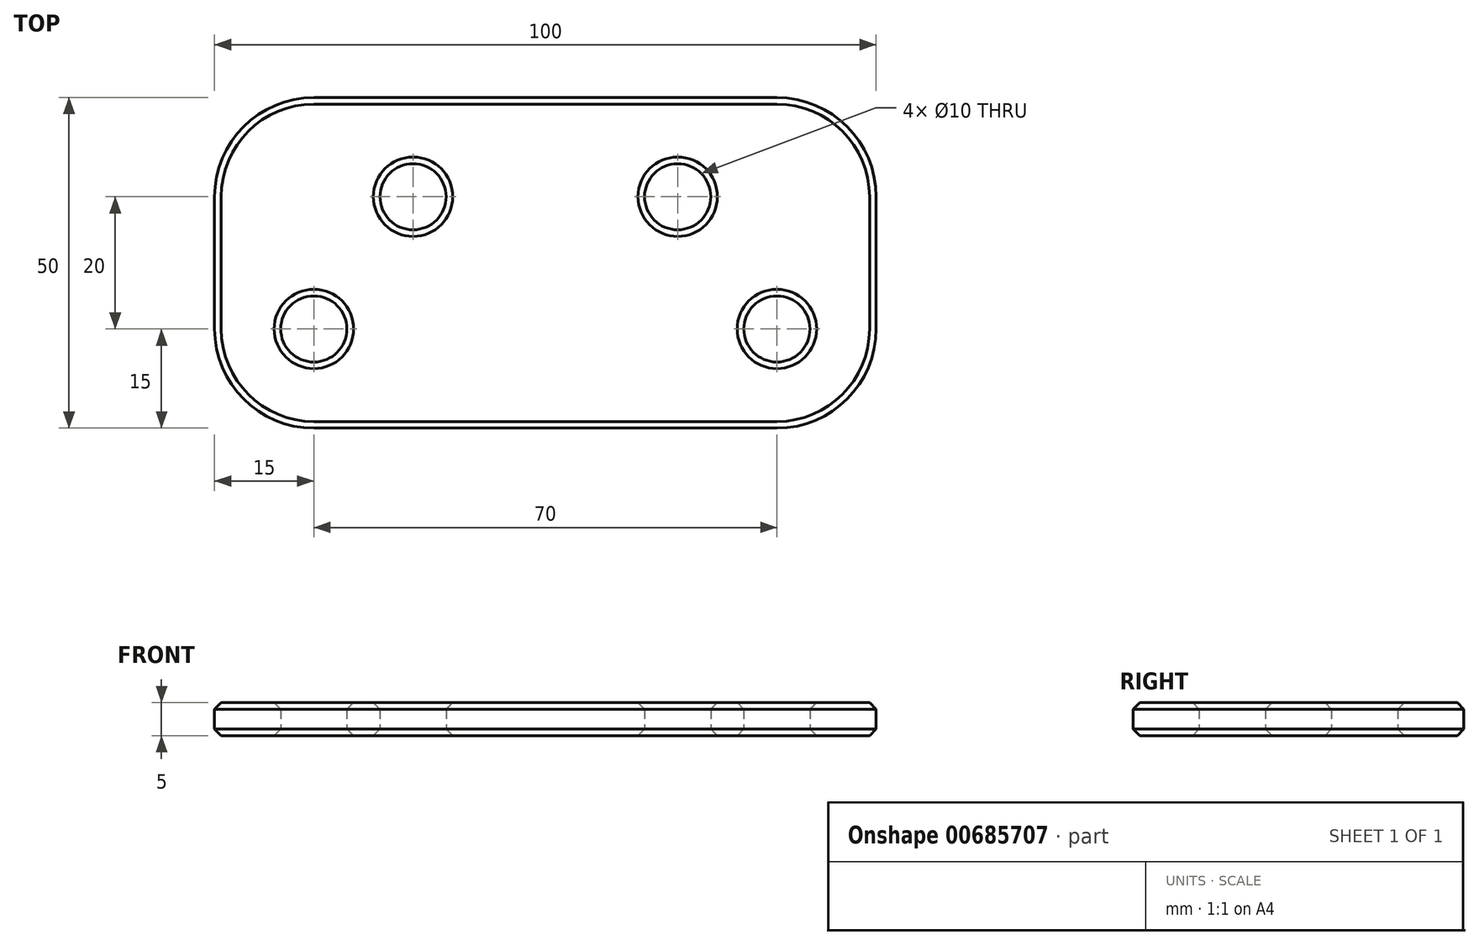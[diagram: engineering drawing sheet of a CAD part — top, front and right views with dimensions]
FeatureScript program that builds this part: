
annotation { "Feature Type Name" : "Feature", "Feature Type Description" : "" }
export const myFeature = defineFeature(function(context is Context, id is Id, definition is map)
    precondition{}
    {
        {
            var Q0;
            Q0=qCreatedBy(makeId("Top.planeOp"),FACE);
            var sketch = newSketch(context, id + "F0", { "sketchPlane" : qUnion([Q0])});
            skLineSegment(sketch, "E0.bottom", {"start": v(50, -25) * mm, "end": v(-50, -25) * mm});
            skLineSegment(sketch, "E0.top", {"start": v(50, 25) * mm, "end": v(-50, 25) * mm});
            skLineSegment(sketch, "E0.left", {"start": v(50, -25) * mm, "end": v(50, 25) * mm});
            skLineSegment(sketch, "E0.right", {"start": v(-50, -25) * mm, "end": v(-50, 25) * mm});
            skPoint(sketch, "E0.middle", {"position": v(0, 0) * mm});
            skLineSegment(sketch, "E1", {"start": v(0, 68.51) * mm, "end": v(0, -45.93) * mm, "construction": true});
            skPoint(sketch, "E1.endSnap0", {"position": v(0, -25) * mm});
            skCircle(sketch, "E2", {"center": v(-20, 10) * mm, "radius": 5 * mm});
            skCircle(sketch, "E3", {"center": v(-35, -10) * mm, "radius": 5 * mm});
            skCircle(sketch, "E4.MirrorC", {"center": v(20, 10) * mm, "radius": 5 * mm});
            skCircle(sketch, "E5.MirrorC", {"center": v(35, -10) * mm, "radius": 5 * mm});
            skSolve(sketch);
        }
        {
            var Q0;
            Q0=makeQuery(id+"F0.imprint","IMPRINT",FACE,{"disambiguationData":[TD([[makeQuery(id+"F0.imprint","IMPRINT",EDGE,{"derivedFrom":sQuery(id+"F0.wireOp",EDGE,"E0.bottom")}),-1.0]])]});
            extrude(context, id + "F1", {"entities" : qUnion([Q0]), "depth" : 5 * mm, "offsetDistance" : 25 * mm});
        }
        {
            var Q0;
            Q0=makeQuery(id+"F1.opExtrude","SWEPT_EDGE",EDGE,{"disambiguationData":[OSD([sQuery(id+"F0.wireOp",EDGE,"E0.top"),sQuery(id+"F0.wireOp",EDGE,"E0.right")])]});
            var Q1;
            Q1=makeQuery(id+"F1.opExtrude","SWEPT_EDGE",EDGE,{"disambiguationData":[OSD([sQuery(id+"F0.wireOp",EDGE,"E0.bottom"),sQuery(id+"F0.wireOp",EDGE,"E0.right")])]});
            var Q2;
            Q2=makeQuery(id+"F1.opExtrude","SWEPT_EDGE",EDGE,{"disambiguationData":[OSD([sQuery(id+"F0.wireOp",EDGE,"E0.bottom"),sQuery(id+"F0.wireOp",EDGE,"E0.left")])]});
            var Q3;
            Q3=makeQuery(id+"F1.opExtrude","SWEPT_EDGE",EDGE,{"disambiguationData":[OSD([sQuery(id+"F0.wireOp",EDGE,"E0.top"),sQuery(id+"F0.wireOp",EDGE,"E0.left")])]});
            fillet(context, id + "F2", {"entities" : qUnion([Q0, Q1, Q2, Q3]), "radius" : 15 * mm, "tangentPropagation" : true, "allowEdgeOverflow" : false});
        }
        {
            var Q0;
            Q0=makeQuery(id+"F1.opExtrude","CAP_EDGE",EDGE,{"disambiguationData":[OSD([sQuery(id+"F0.wireOp",EDGE,"E2")])],"isStart":false});
            var Q1;
            Q1=makeQuery(id+"F1.opExtrude","CAP_EDGE",EDGE,{"disambiguationData":[OSD([sQuery(id+"F0.wireOp",EDGE,"E3")])],"isStart":false});
            var Q2;
            Q2=makeQuery(id+"F1.opExtrude","CAP_EDGE",EDGE,{"disambiguationData":[OSD([sQuery(id+"F0.wireOp",EDGE,"E2")])],"isStart":true});
            var Q3;
            Q3=makeQuery(id+"F1.opExtrude","CAP_EDGE",EDGE,{"disambiguationData":[OSD([sQuery(id+"F0.wireOp",EDGE,"E3")])],"isStart":true});
            var Q4;
            Q4=makeQuery(id+"F1.opExtrude","CAP_EDGE",EDGE,{"disambiguationData":[OSD([sQuery(id+"F0.wireOp",EDGE,"E4.MirrorC")])],"isStart":false});
            var Q5;
            Q5=makeQuery(id+"F1.opExtrude","CAP_EDGE",EDGE,{"disambiguationData":[OSD([sQuery(id+"F0.wireOp",EDGE,"E4.MirrorC")])],"isStart":true});
            var Q6;
            Q6=makeQuery(id+"F1.opExtrude","CAP_EDGE",EDGE,{"disambiguationData":[OSD([sQuery(id+"F0.wireOp",EDGE,"E5.MirrorC")])],"isStart":false});
            var Q7;
            Q7=makeQuery(id+"F1.opExtrude","CAP_EDGE",EDGE,{"disambiguationData":[OSD([sQuery(id+"F0.wireOp",EDGE,"E5.MirrorC")])],"isStart":true});
            chamfer(context, id + "F3", {"entities" : qUnion([Q0, Q1, Q2, Q3, Q4, Q5, Q6, Q7]), "width" : 1 * mm, "tangentPropagation" : true});
        }
        {
            var Q0;
            {var subQ0=sQuery(id+"F0.wireOp",EDGE,"E0.right");var subQ1=sQuery(id+"F0.wireOp",EDGE,"E0.top");Q0=makeQuery(id+"F2.opFillet","BLEND_EDGE",EDGE,{"blendedFrom":[makeQuery(id+"F1.opExtrude","SWEPT_EDGE",EDGE,{"disambiguationData":[OSD([subQ1,subQ0])]}),makeQuery(id+"F1.opExtrude","CAP_FACE",FACE,{"disambiguationData":[OSD([sQuery(id+"F0.wireOp",EDGE,"E0.bottom"),subQ1,sQuery(id+"F0.wireOp",EDGE,"E0.left"),subQ0,sQuery(id+"F0.wireOp",EDGE,"E2"),sQuery(id+"F0.wireOp",EDGE,"E3"),sQuery(id+"F0.wireOp",EDGE,"E4.MirrorC"),sQuery(id+"F0.wireOp",EDGE,"E5.MirrorC")])],"isStart":false})],"blendedInto":[makeQuery(id+"F1.opExtrude","CAP_FACE",FACE,{"disambiguationData":[OSD([sQuery(id+"F0.wireOp",EDGE,"E0.bottom"),subQ1,sQuery(id+"F0.wireOp",EDGE,"E0.left"),subQ0,sQuery(id+"F0.wireOp",EDGE,"E2"),sQuery(id+"F0.wireOp",EDGE,"E3"),sQuery(id+"F0.wireOp",EDGE,"E4.MirrorC"),sQuery(id+"F0.wireOp",EDGE,"E5.MirrorC")])],"isStart":false})]});}
            var Q1;
            Q1=makeQuery(id+"F1.opExtrude","CAP_EDGE",EDGE,{"disambiguationData":[OSD([sQuery(id+"F0.wireOp",EDGE,"E0.right")])],"isStart":true});
            chamfer(context, id + "F4", {"entities" : qUnion([Q0, Q1]), "width" : 1 * mm, "tangentPropagation" : true});
        }
    });
